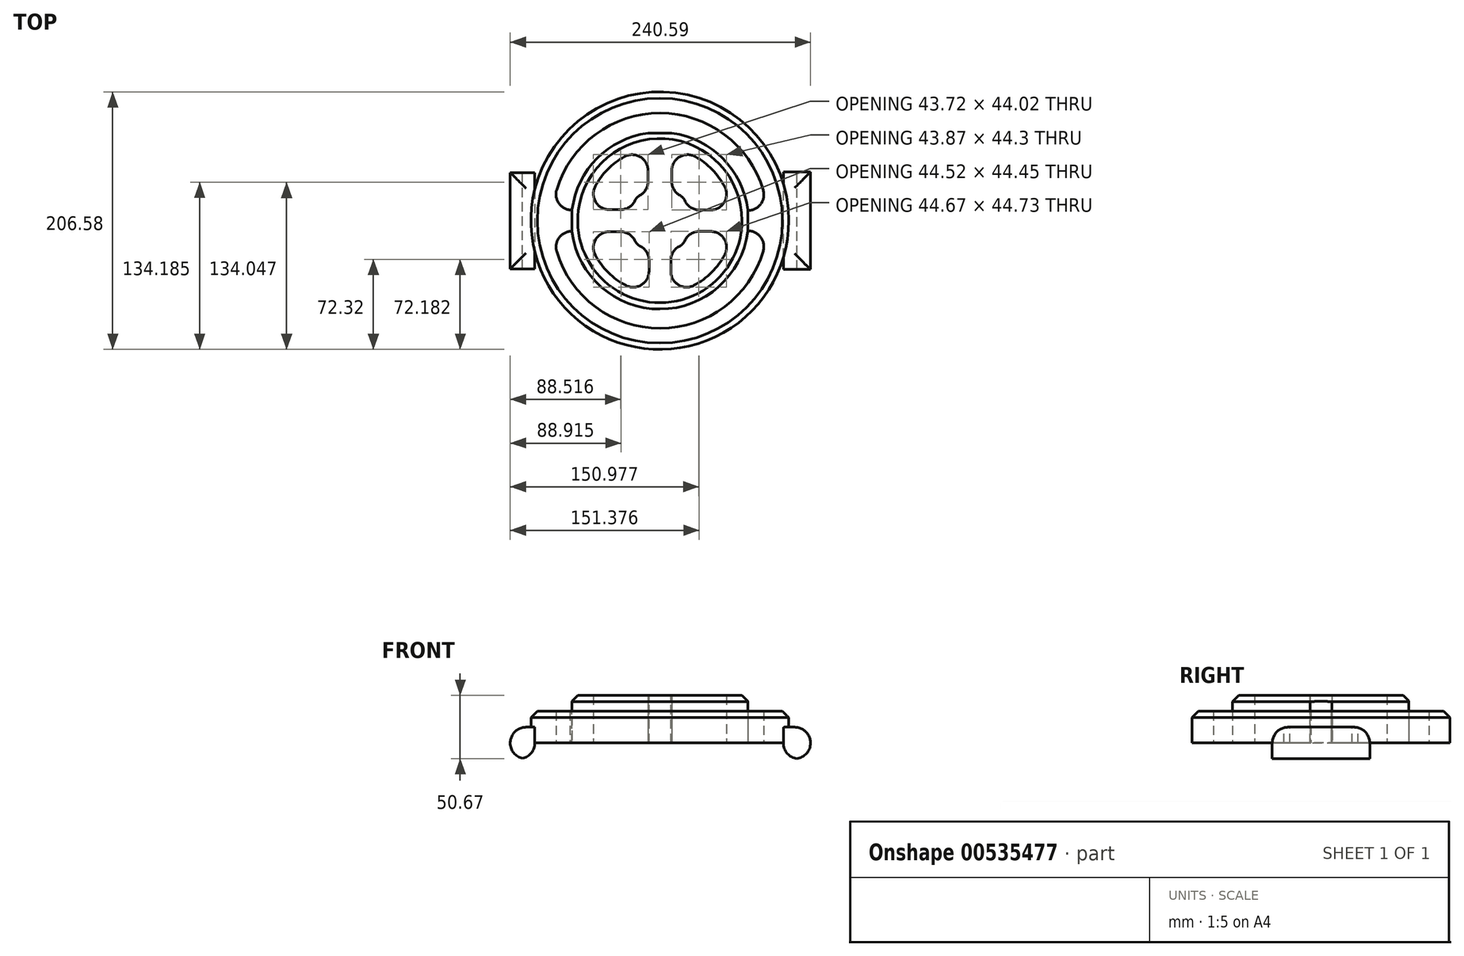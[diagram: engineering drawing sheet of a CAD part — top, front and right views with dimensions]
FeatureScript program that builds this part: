
annotation { "Feature Type Name" : "Feature", "Feature Type Description" : "" }
export const myFeature = defineFeature(function(context is Context, id is Id, definition is map)
    precondition{}
    {
        {
            var Q0;
            Q0=qCreatedBy(makeId("Top.planeOp"),FACE);
            var sketch = newSketch(context, id + "F0", { "sketchPlane" : qUnion([Q0])});
            skCircle(sketch, "E0", {"center": v(0, 0) * mm, "radius": 70.91 * mm});
            skCircle(sketch, "E1", {"center": v(0, 0) * mm, "radius": 58.64 * mm});
            skLineSegment(sketch, "E2.bottom", {"start": v(20.75, 21.47) * mm, "end": v(-20.75, 21.47) * mm});
            skLineSegment(sketch, "E2.top", {"start": v(20.75, -21.47) * mm, "end": v(-20.75, -21.47) * mm});
            skLineSegment(sketch, "E2.left", {"start": v(20.75, 21.47) * mm, "end": v(20.75, -21.47) * mm});
            skLineSegment(sketch, "E2.right", {"start": v(-20.75, 21.47) * mm, "end": v(-20.75, -21.47) * mm});
            skLineSegment(sketch, "E3.bottom", {"start": v(70.4, 8.6) * mm, "end": v(14.78, 8.6) * mm});
            skLineSegment(sketch, "E3.top", {"start": v(70.4, -8.6) * mm, "end": v(14.78, -8.6) * mm});
            skLineSegment(sketch, "E3.left", {"start": v(70.4, 8.6) * mm, "end": v(70.4, -8.6) * mm});
            skLineSegment(sketch, "E3.right", {"start": v(14.78, 8.6) * mm, "end": v(14.78, -8.6) * mm});
            skPoint(sketch, "E3.middle", {"position": v(42.58, 0) * mm});
            skLineSegment(sketch, "E4.bottom", {"start": v(9.53, 70.27) * mm, "end": v(-9.53, 70.27) * mm});
            skLineSegment(sketch, "E4.top", {"start": v(9.53, 11.29) * mm, "end": v(-9.53, 11.29) * mm});
            skLineSegment(sketch, "E4.left", {"start": v(9.53, 70.27) * mm, "end": v(9.53, 11.29) * mm});
            skLineSegment(sketch, "E4.right", {"start": v(-9.53, 70.27) * mm, "end": v(-9.53, 11.29) * mm});
            skPoint(sketch, "E4.middle", {"position": v(0, 40.78) * mm});
            skLineSegment(sketch, "E5.bottom", {"start": v(-70.36, -8.88) * mm, "end": v(-4.76, -8.88) * mm});
            skLineSegment(sketch, "E5.top", {"start": v(-70.36, 8.88) * mm, "end": v(-4.76, 8.88) * mm});
            skLineSegment(sketch, "E5.left", {"start": v(-70.36, -8.88) * mm, "end": v(-70.36, 8.88) * mm});
            skLineSegment(sketch, "E5.right", {"start": v(-4.76, -8.88) * mm, "end": v(-4.76, 8.88) * mm});
            skPoint(sketch, "E5.middle", {"position": v(-37.56, 0) * mm});
            skLineSegment(sketch, "E6.bottom", {"start": v(8.73, -9.64) * mm, "end": v(-8.73, -9.64) * mm});
            skLineSegment(sketch, "E6.top", {"start": v(8.73, -62.55) * mm, "end": v(-8.73, -62.55) * mm});
            skLineSegment(sketch, "E6.left", {"start": v(8.73, -9.64) * mm, "end": v(8.73, -62.55) * mm});
            skLineSegment(sketch, "E6.right", {"start": v(-8.73, -9.64) * mm, "end": v(-8.73, -62.55) * mm});
            skPoint(sketch, "E6.middle", {"position": v(0, -36.1) * mm});
            skPoint(sketch, "E6.middle.positionSnap0", {"position": v(0, -21.47) * mm});
            skPoint(sketch, "E6.centerSnap0", {"position": v(0, -21.47) * mm});
            skSolve(sketch);
        }
        {
            var Q0;
            {var subQ0=sQuery(id+"F0.wireOp",EDGE,"E4.left");var subQ1=sQuery(id+"F0.wireOp",EDGE,"E1");var subQ2=makeQuery(id+"F0.imprint","INTERSECT",VERTEX,{"derivedFrom":[subQ1,subQ0]});Q0=makeQuery(id+"F0.imprint","IMPRINT",FACE,{"disambiguationData":[TD([[makeQuery(id+"F0.imprint","IMPRINT",EDGE,{"disambiguationData":[TD([[subQ2,-1.0]])],"derivedFrom":subQ1}),1.0]])]});}
            var Q1;
            {var subQ5=sQuery(id+"F0.wireOp",EDGE,"E4.bottom");Q1=makeQuery(id+"F0.imprint","IMPRINT",FACE,{"disambiguationData":[TD([[makeQuery(id+"F0.imprint","IMPRINT",EDGE,{"derivedFrom":subQ5}),1.0]])]});}
            var Q2;
            {var subQ3=sQuery(id+"F0.wireOp",EDGE,"E4.left");var subQ5=sQuery(id+"F0.wireOp",EDGE,"E1");var subQ6=makeQuery(id+"F0.imprint","INTERSECT",VERTEX,{"derivedFrom":[subQ5,subQ3]});Q2=makeQuery(id+"F0.imprint","IMPRINT",FACE,{"disambiguationData":[TD([[makeQuery(id+"F0.imprint","IMPRINT",EDGE,{"disambiguationData":[TD([[subQ6,1.0]])],"derivedFrom":subQ5}),-1.0]])]});}
            var Q3;
            {var subQ0=sQuery(id+"F0.wireOp",EDGE,"E4.right");var subQ5=sQuery(id+"F0.wireOp",EDGE,"E1");var subQ6=makeQuery(id+"F0.imprint","INTERSECT",VERTEX,{"derivedFrom":[subQ5,subQ0]});Q3=makeQuery(id+"F0.imprint","IMPRINT",FACE,{"disambiguationData":[TD([[makeQuery(id+"F0.imprint","IMPRINT",EDGE,{"disambiguationData":[TD([[subQ6,-1.0]])],"derivedFrom":subQ5}),-1.0]])]});}
            var Q4;
            {var subQ9=sQuery(id+"F0.wireOp",EDGE,"E6.top");Q4=makeQuery(id+"F0.imprint","IMPRINT",FACE,{"disambiguationData":[TD([[makeQuery(id+"F0.imprint","IMPRINT",EDGE,{"derivedFrom":subQ9}),1.0]])]});}
            var Q5;
            {var subQ0=sQuery(id+"F0.wireOp",EDGE,"E6.right");var subQ1=sQuery(id+"F0.wireOp",EDGE,"E1");var subQ2=makeQuery(id+"F0.imprint","INTERSECT",VERTEX,{"derivedFrom":[subQ1,subQ0]});Q5=makeQuery(id+"F0.imprint","IMPRINT",FACE,{"disambiguationData":[TD([[makeQuery(id+"F0.imprint","IMPRINT",EDGE,{"disambiguationData":[TD([[subQ2,-1.0]])],"derivedFrom":subQ1}),1.0]])]});}
            var Q6;
            {var subQ5=sQuery(id+"F0.wireOp",EDGE,"E6.top");Q6=makeQuery(id+"F0.imprint","IMPRINT",FACE,{"disambiguationData":[TD([[makeQuery(id+"F0.imprint","IMPRINT",EDGE,{"derivedFrom":subQ5}),-1.0]])]});}
            var Q7;
            {var subQ5=sQuery(id+"F0.wireOp",EDGE,"E6.bottom");Q7=makeQuery(id+"F0.imprint","IMPRINT",FACE,{"disambiguationData":[TD([[makeQuery(id+"F0.imprint","IMPRINT",EDGE,{"derivedFrom":subQ5}),1.0]])]});}
            var Q8;
            {var subQ10=sQuery(id+"F0.wireOp",EDGE,"E3.right");Q8=makeQuery(id+"F0.imprint","IMPRINT",FACE,{"disambiguationData":[TD([[makeQuery(id+"F0.imprint","IMPRINT",EDGE,{"derivedFrom":subQ10}),-1.0]])]});}
            var Q9;
            {var subQ5=sQuery(id+"F0.wireOp",EDGE,"E5.right");Q9=makeQuery(id+"F0.imprint","IMPRINT",FACE,{"disambiguationData":[TD([[makeQuery(id+"F0.imprint","IMPRINT",EDGE,{"derivedFrom":subQ5}),1.0]])]});}
            var Q10;
            {var subQ5=sQuery(id+"F0.wireOp",EDGE,"E4.top");Q10=makeQuery(id+"F0.imprint","IMPRINT",FACE,{"disambiguationData":[TD([[makeQuery(id+"F0.imprint","IMPRINT",EDGE,{"derivedFrom":subQ5}),-1.0]])]});}
            var Q11;
            {var subQ0=sQuery(id+"F0.wireOp",EDGE,"E3.bottom");var subQ1=sQuery(id+"F0.wireOp",EDGE,"E1");var subQ2=makeQuery(id+"F0.imprint","INTERSECT",VERTEX,{"derivedFrom":[subQ1,subQ0]});Q11=makeQuery(id+"F0.imprint","IMPRINT",FACE,{"disambiguationData":[TD([[makeQuery(id+"F0.imprint","IMPRINT",EDGE,{"disambiguationData":[TD([[subQ2,1.0]])],"derivedFrom":subQ1}),1.0]])]});}
            var Q12;
            {var subQ5=sQuery(id+"F0.wireOp",EDGE,"E3.right");Q12=makeQuery(id+"F0.imprint","IMPRINT",FACE,{"disambiguationData":[TD([[makeQuery(id+"F0.imprint","IMPRINT",EDGE,{"derivedFrom":subQ5}),1.0]])]});}
            var Q13;
            {var subQ5=sQuery(id+"F0.wireOp",EDGE,"E3.left");Q13=makeQuery(id+"F0.imprint","IMPRINT",FACE,{"disambiguationData":[TD([[makeQuery(id+"F0.imprint","IMPRINT",EDGE,{"derivedFrom":subQ5}),-1.0]])]});}
            var Q14;
            {var subQ5=sQuery(id+"F0.wireOp",EDGE,"E5.left");Q14=makeQuery(id+"F0.imprint","IMPRINT",FACE,{"disambiguationData":[TD([[makeQuery(id+"F0.imprint","IMPRINT",EDGE,{"derivedFrom":subQ5}),-1.0]])]});}
            var Q15;
            {var subQ0=sQuery(id+"F0.wireOp",EDGE,"E5.top");var subQ1=sQuery(id+"F0.wireOp",EDGE,"E1");var subQ2=makeQuery(id+"F0.imprint","INTERSECT",VERTEX,{"derivedFrom":[subQ1,subQ0]});Q15=makeQuery(id+"F0.imprint","IMPRINT",FACE,{"disambiguationData":[TD([[makeQuery(id+"F0.imprint","IMPRINT",EDGE,{"disambiguationData":[TD([[subQ2,-1.0]])],"derivedFrom":subQ1}),1.0]])]});}
            extrude(context, id + "F1", {"entities" : qUnion([Q0, Q1, Q2, Q3, Q4, Q5, Q6, Q7, Q8, Q9, Q10, Q11, Q12, Q13, Q14, Q15]), "depth" : 25.4 * mm, "offsetDistance" : 25.4 * mm});
        }
        {
            var Q0;
            Q0=qCreatedBy(makeId("Top.planeOp"),FACE);
            var sketch = newSketch(context, id + "F2", { "sketchPlane" : qUnion([Q0])});
            skCircle(sketch, "E7", {"center": v(0, 0) * mm, "radius": 86.33 * mm});
            skCircle(sketch, "E8", {"center": v(0, 0) * mm, "radius": 103.3 * mm});
            skLineSegment(sketch, "E9.bottom", {"start": v(94.37, 8.12) * mm, "end": v(61.17, 8.12) * mm});
            skLineSegment(sketch, "E9.top", {"start": v(94.37, -8.12) * mm, "end": v(61.17, -8.12) * mm});
            skLineSegment(sketch, "E9.left", {"start": v(94.37, 8.12) * mm, "end": v(94.37, -8.12) * mm});
            skLineSegment(sketch, "E9.right", {"start": v(61.17, 8.12) * mm, "end": v(61.17, -8.12) * mm});
            skPoint(sketch, "E9.middle", {"position": v(77.77, 0) * mm});
            skLineSegment(sketch, "E10.bottom", {"start": v(-59.19, 8.48) * mm, "end": v(-96, 8.48) * mm});
            skLineSegment(sketch, "E10.top", {"start": v(-59.19, -8.48) * mm, "end": v(-96, -8.48) * mm});
            skLineSegment(sketch, "E10.left", {"start": v(-59.19, 8.48) * mm, "end": v(-59.19, -8.48) * mm});
            skLineSegment(sketch, "E10.right", {"start": v(-96, 8.48) * mm, "end": v(-96, -8.48) * mm});
            skPoint(sketch, "E10.middle", {"position": v(-77.6, 0) * mm});
            skSolve(sketch);
        }
        {
            var Q0;
            Q0=makeQuery(id+"F2.imprint","IMPRINT",FACE,{"disambiguationData":[TD([[makeQuery(id+"F2.imprint","IMPRINT",EDGE,{"derivedFrom":sQuery(id+"F2.wireOp",EDGE,"E8")}),1.0]])]});
            var Q1;
            {var subQ5=sQuery(id+"F2.wireOp",EDGE,"E9.left");Q1=makeQuery(id+"F2.imprint","IMPRINT",FACE,{"disambiguationData":[TD([[makeQuery(id+"F2.imprint","IMPRINT",EDGE,{"derivedFrom":subQ5}),-1.0]])]});}
            var Q2;
            {var subQ5=sQuery(id+"F2.wireOp",EDGE,"E9.right");Q2=makeQuery(id+"F2.imprint","IMPRINT",FACE,{"disambiguationData":[TD([[makeQuery(id+"F2.imprint","IMPRINT",EDGE,{"derivedFrom":subQ5}),1.0]])]});}
            var Q3;
            {var subQ5=sQuery(id+"F2.wireOp",EDGE,"E10.left");Q3=makeQuery(id+"F2.imprint","IMPRINT",FACE,{"disambiguationData":[TD([[makeQuery(id+"F2.imprint","IMPRINT",EDGE,{"derivedFrom":subQ5}),-1.0]])]});}
            var Q4;
            {var subQ5=sQuery(id+"F2.wireOp",EDGE,"E10.right");Q4=makeQuery(id+"F2.imprint","IMPRINT",FACE,{"disambiguationData":[TD([[makeQuery(id+"F2.imprint","IMPRINT",EDGE,{"derivedFrom":subQ5}),1.0]])]});}
            extrude(context, id + "F3", {"entities" : qUnion([Q0, Q1, Q2, Q3, Q4]), "operationType" : NewBodyOperationType.ADD, "depth" : 12.7 * mm, "offsetDistance" : 25.4 * mm});
        }
        {
            var Q0;
            Q0=makeQuery(id+"F1.opExtrude","SWEPT_EDGE",EDGE,{"disambiguationData":[OSD([sQuery(id+"F0.wireOp",EDGE,"E2.top"),sQuery(id+"F0.wireOp",EDGE,"E2.right")])]});
            var Q1;
            Q1=makeQuery(id+"F1.opExtrude","SWEPT_EDGE",EDGE,{"disambiguationData":[OSD([sQuery(id+"F0.wireOp",EDGE,"E2.top"),sQuery(id+"F0.wireOp",EDGE,"E2.left")])]});
            var Q2;
            Q2=makeQuery(id+"F1.opExtrude","SWEPT_EDGE",EDGE,{"disambiguationData":[OSD([sQuery(id+"F0.wireOp",EDGE,"E2.bottom"),sQuery(id+"F0.wireOp",EDGE,"E2.left")])]});
            var Q3;
            Q3=makeQuery(id+"F1.opExtrude","SWEPT_EDGE",EDGE,{"disambiguationData":[OSD([sQuery(id+"F0.wireOp",EDGE,"E2.bottom"),sQuery(id+"F0.wireOp",EDGE,"E2.right")])]});
            fillet(context, id + "F4", {"entities" : qUnion([Q0, Q1, Q2, Q3]), "radius" : 9.16 * mm, "tangentPropagation" : true, "allowEdgeOverflow" : false});
        }
        {
            var Q0;
            Q0=makeQuery(id+"F1.opExtrude","SWEPT_EDGE",EDGE,{"disambiguationData":[OSD([sQuery(id+"F0.wireOp",EDGE,"E1"),sQuery(id+"F0.wireOp",EDGE,"E4.left")])]});
            var Q1;
            Q1=makeQuery(id+"F1.opExtrude","SWEPT_EDGE",EDGE,{"disambiguationData":[OSD([sQuery(id+"F0.wireOp",EDGE,"E1"),sQuery(id+"F0.wireOp",EDGE,"E3.bottom")])]});
            var Q2;
            Q2=makeQuery(id+"F1.opExtrude","SWEPT_EDGE",EDGE,{"disambiguationData":[OSD([sQuery(id+"F0.wireOp",EDGE,"E1"),sQuery(id+"F0.wireOp",EDGE,"E4.right")])]});
            var Q3;
            Q3=makeQuery(id+"F1.opExtrude","SWEPT_EDGE",EDGE,{"disambiguationData":[OSD([sQuery(id+"F0.wireOp",EDGE,"E1"),sQuery(id+"F0.wireOp",EDGE,"E5.top")])]});
            var Q4;
            Q4=makeQuery(id+"F1.opExtrude","SWEPT_EDGE",EDGE,{"disambiguationData":[OSD([sQuery(id+"F0.wireOp",EDGE,"E1"),sQuery(id+"F0.wireOp",EDGE,"E3.top")])]});
            var Q5;
            Q5=makeQuery(id+"F1.opExtrude","SWEPT_EDGE",EDGE,{"disambiguationData":[OSD([sQuery(id+"F0.wireOp",EDGE,"E1"),sQuery(id+"F0.wireOp",EDGE,"E6.left")])]});
            var Q6;
            Q6=makeQuery(id+"F1.opExtrude","SWEPT_EDGE",EDGE,{"disambiguationData":[OSD([sQuery(id+"F0.wireOp",EDGE,"E1"),sQuery(id+"F0.wireOp",EDGE,"E5.bottom")])]});
            var Q7;
            Q7=makeQuery(id+"F1.opExtrude","SWEPT_EDGE",EDGE,{"disambiguationData":[OSD([sQuery(id+"F0.wireOp",EDGE,"E1"),sQuery(id+"F0.wireOp",EDGE,"E6.right")])]});
            var Q8;
            Q8=makeQuery(id+"F1.opExtrude","SWEPT_EDGE",EDGE,{"disambiguationData":[OSD([sQuery(id+"F0.wireOp",EDGE,"E2.right"),sQuery(id+"F0.wireOp",EDGE,"E5.bottom")])]});
            var Q9;
            Q9=makeQuery(id+"F1.opExtrude","SWEPT_EDGE",EDGE,{"disambiguationData":[OSD([sQuery(id+"F0.wireOp",EDGE,"E2.top"),sQuery(id+"F0.wireOp",EDGE,"E6.right")])]});
            var Q10;
            Q10=makeQuery(id+"F1.opExtrude","SWEPT_EDGE",EDGE,{"disambiguationData":[OSD([sQuery(id+"F0.wireOp",EDGE,"E2.left"),sQuery(id+"F0.wireOp",EDGE,"E3.top")])]});
            var Q11;
            Q11=makeQuery(id+"F1.opExtrude","SWEPT_EDGE",EDGE,{"disambiguationData":[OSD([sQuery(id+"F0.wireOp",EDGE,"E2.top"),sQuery(id+"F0.wireOp",EDGE,"E6.left")])]});
            var Q12;
            Q12=makeQuery(id+"F1.opExtrude","SWEPT_EDGE",EDGE,{"disambiguationData":[OSD([sQuery(id+"F0.wireOp",EDGE,"E2.bottom"),sQuery(id+"F0.wireOp",EDGE,"E4.left")])]});
            var Q13;
            Q13=makeQuery(id+"F1.opExtrude","SWEPT_EDGE",EDGE,{"disambiguationData":[OSD([sQuery(id+"F0.wireOp",EDGE,"E2.left"),sQuery(id+"F0.wireOp",EDGE,"E3.bottom")])]});
            var Q14;
            Q14=makeQuery(id+"F1.opExtrude","SWEPT_EDGE",EDGE,{"disambiguationData":[OSD([sQuery(id+"F0.wireOp",EDGE,"E2.right"),sQuery(id+"F0.wireOp",EDGE,"E5.top")])]});
            var Q15;
            Q15=makeQuery(id+"F1.opExtrude","SWEPT_EDGE",EDGE,{"disambiguationData":[OSD([sQuery(id+"F0.wireOp",EDGE,"E2.bottom"),sQuery(id+"F0.wireOp",EDGE,"E4.right")])]});
            var Q16;
            Q16=makeQuery(id+"F3.opExtrude","SWEPT_EDGE",EDGE,{"disambiguationData":[OSD([sQuery(id+"F2.wireOp",EDGE,"E7"),sQuery(id+"F2.wireOp",EDGE,"E9.top")])]});
            var Q17;
            Q17=makeQuery(id+"F3.opExtrude","SWEPT_EDGE",EDGE,{"disambiguationData":[OSD([sQuery(id+"F2.wireOp",EDGE,"E7"),sQuery(id+"F2.wireOp",EDGE,"E10.top")])]});
            var Q18;
            Q18=makeQuery(id+"F3.boolean.opBoolean","INTERSECT",EDGE,{"derivedFrom":[makeQuery(id+"F1.opExtrude","SWEPT_FACE",FACE,{"disambiguationData":[OSD([sQuery(id+"F0.wireOp",EDGE,"E5.left")])]}),makeQuery(id+"F3.opExtrude","SWEPT_FACE",FACE,{"disambiguationData":[OSD([sQuery(id+"F2.wireOp",EDGE,"E10.top")])]})]});
            var Q19;
            Q19=makeQuery(id+"F3.opExtrude","SWEPT_EDGE",EDGE,{"disambiguationData":[OSD([sQuery(id+"F2.wireOp",EDGE,"E7"),sQuery(id+"F2.wireOp",EDGE,"E10.bottom")])]});
            var Q20;
            Q20=makeQuery(id+"F3.opExtrude","SWEPT_EDGE",EDGE,{"disambiguationData":[OSD([sQuery(id+"F2.wireOp",EDGE,"E7"),sQuery(id+"F2.wireOp",EDGE,"E9.bottom")])]});
            fillet(context, id + "F5", {"entities" : qUnion([Q0, Q1, Q2, Q3, Q4, Q5, Q6, Q7, Q8, Q9, Q10, Q11, Q12, Q13, Q14, Q15, Q16, Q17, Q18, Q19, Q20]), "radius" : 12.7 * mm, "tangentPropagation" : true, "allowEdgeOverflow" : false});
        }
        {
            var Q0;
            Q0=qCreatedBy(makeId("Top.planeOp"),FACE);
            var sketch = newSketch(context, id + "F6", { "sketchPlane" : qUnion([Q0])});
            skLineSegment(sketch, "E11.bottom", {"start": v(120.68, -39.1) * mm, "end": v(98.93, -39.1) * mm});
            skLineSegment(sketch, "E11.top", {"start": v(120.68, 39.1) * mm, "end": v(98.93, 39.1) * mm});
            skLineSegment(sketch, "E11.left", {"start": v(120.68, -39.1) * mm, "end": v(120.68, 39.1) * mm});
            skLineSegment(sketch, "E11.right", {"start": v(98.93, -39.1) * mm, "end": v(98.93, 39.1) * mm});
            skPoint(sketch, "E11.middle", {"position": v(109.8, 0) * mm});
            skLineSegment(sketch, "E12.bottom", {"start": v(-119.9, 38.59) * mm, "end": v(-100.22, 38.59) * mm});
            skLineSegment(sketch, "E12.top", {"start": v(-119.9, -38.59) * mm, "end": v(-100.22, -38.59) * mm});
            skLineSegment(sketch, "E12.left", {"start": v(-119.9, 38.59) * mm, "end": v(-119.9, -38.59) * mm});
            skLineSegment(sketch, "E12.right", {"start": v(-100.22, 38.59) * mm, "end": v(-100.22, -38.59) * mm});
            skPoint(sketch, "E12.middle", {"position": v(-110.07, 0) * mm});
            skSolve(sketch);
        }
        {
            var Q0;
            Q0=makeQuery(id+"F6.imprint","IMPRINT",FACE,{"disambiguationData":[TD([[makeQuery(id+"F6.imprint","IMPRINT",EDGE,{"derivedFrom":sQuery(id+"F6.wireOp",EDGE,"E11.bottom")}),-1.0]])]});
            var Q1;
            Q1=makeQuery(id+"F6.imprint","IMPRINT",FACE,{"disambiguationData":[TD([[makeQuery(id+"F6.imprint","IMPRINT",EDGE,{"derivedFrom":sQuery(id+"F6.wireOp",EDGE,"E12.bottom")}),-1.0]])]});
            extrude(context, id + "F7", {"entities" : qUnion([Q0, Q1]), "operationType" : NewBodyOperationType.ADD, "oppositeDirection" : true, "depth" : 25.4 * mm, "offsetDistance" : 25.4 * mm});
        }
        {
            var Q0;
            Q0=makeQuery(id+"F7.opExtrude","CAP_EDGE",EDGE,{"disambiguationData":[OSD([sQuery(id+"F6.wireOp",EDGE,"E12.left")])],"isStart":false});
            var Q1;
            Q1=makeQuery(id+"F7.opExtrude","CAP_EDGE",EDGE,{"disambiguationData":[OSD([sQuery(id+"F6.wireOp",EDGE,"E12.right")])],"isStart":false});
            var Q2;
            Q2=makeQuery(id+"F7.opExtrude","CAP_EDGE",EDGE,{"disambiguationData":[OSD([sQuery(id+"F6.wireOp",EDGE,"E12.bottom")])],"isStart":true});
            var Q3;
            Q3=makeQuery(id+"F7.opExtrude","CAP_EDGE",EDGE,{"disambiguationData":[OSD([sQuery(id+"F6.wireOp",EDGE,"E12.top")])],"isStart":true});
            var Q4;
            Q4=makeQuery(id+"F7.opExtrude","CAP_EDGE",EDGE,{"disambiguationData":[OSD([sQuery(id+"F6.wireOp",EDGE,"E12.left")])],"isStart":true});
            var Q5;
            Q5=makeQuery(id+"F7.opExtrude","CAP_EDGE",EDGE,{"disambiguationData":[OSD([sQuery(id+"F6.wireOp",EDGE,"E11.right")])],"isStart":false});
            var Q6;
            Q6=makeQuery(id+"F7.opExtrude","CAP_EDGE",EDGE,{"disambiguationData":[OSD([sQuery(id+"F6.wireOp",EDGE,"E11.left")])],"isStart":false});
            var Q7;
            Q7=makeQuery(id+"F7.opExtrude","CAP_EDGE",EDGE,{"disambiguationData":[OSD([sQuery(id+"F6.wireOp",EDGE,"E11.bottom")])],"isStart":true});
            var Q8;
            Q8=makeQuery(id+"F7.opExtrude","CAP_EDGE",EDGE,{"disambiguationData":[OSD([sQuery(id+"F6.wireOp",EDGE,"E11.left")])],"isStart":true});
            var Q9;
            Q9=makeQuery(id+"F7.opExtrude","CAP_EDGE",EDGE,{"disambiguationData":[OSD([sQuery(id+"F6.wireOp",EDGE,"E11.top")])],"isStart":true});
            fillet(context, id + "F8", {"entities" : qUnion([Q0, Q1, Q2, Q3, Q4, Q5, Q6, Q7, Q8, Q9]), "radius" : 12.7 * mm, "tangentPropagation" : true, "allowEdgeOverflow" : false});
        }
        {
            var Q0;
            Q0=makeQuery(id+"F3.opExtrude","CAP_EDGE",EDGE,{"disambiguationData":[OSD([sQuery(id+"F2.wireOp",EDGE,"E8")])],"isStart":false});
            var Q1;
            {var subQ0=sQuery(id+"F0.wireOp",EDGE,"E0");Q1=makeQuery(id+"F1.opExtrude","CAP_EDGE",EDGE,{"disambiguationData":[OSD([subQ0]),TDD([makeQuery(id+"F0.imprint","IMPRINT",EDGE,{"disambiguationData":[TD([[makeQuery(id+"F0.imprint","INTERSECT",VERTEX,{"derivedFrom":[subQ0,sQuery(id+"F0.wireOp",EDGE,"E3.bottom"),sQuery(id+"F0.wireOp",EDGE,"E3.left")]}),-1.0]])],"derivedFrom":subQ0})])],"isStart":false});}
            chamfer(context, id + "F9", {"entities" : qUnion([Q0, Q1]), "width" : 5.08 * mm, "tangentPropagation" : true});
        }
        {
            var Q0;
            Q0=makeQuery(id+"F3.boolean.opBoolean","MERGE",FACE,{"derivedFrom":[makeQuery(id+"F1.opExtrude","CAP_FACE",FACE,{"disambiguationData":[OSD([sQuery(id+"F0.wireOp",EDGE,"E0"),sQuery(id+"F0.wireOp",EDGE,"E1"),sQuery(id+"F0.wireOp",EDGE,"E2.bottom"),sQuery(id+"F0.wireOp",EDGE,"E2.top"),sQuery(id+"F0.wireOp",EDGE,"E2.left"),sQuery(id+"F0.wireOp",EDGE,"E2.right"),sQuery(id+"F0.wireOp",EDGE,"E3.bottom"),sQuery(id+"F0.wireOp",EDGE,"E3.top"),sQuery(id+"F0.wireOp",EDGE,"E3.left"),sQuery(id+"F0.wireOp",EDGE,"E4.bottom"),sQuery(id+"F0.wireOp",EDGE,"E4.left"),sQuery(id+"F0.wireOp",EDGE,"E4.right"),sQuery(id+"F0.wireOp",EDGE,"E5.bottom"),sQuery(id+"F0.wireOp",EDGE,"E5.top"),sQuery(id+"F0.wireOp",EDGE,"E5.left"),sQuery(id+"F0.wireOp",EDGE,"E6.left"),sQuery(id+"F0.wireOp",EDGE,"E6.right")])],"isStart":true}),makeQuery(id+"F3.opExtrude","CAP_FACE",FACE,{"disambiguationData":[OSD([sQuery(id+"F2.wireOp",EDGE,"E7"),sQuery(id+"F2.wireOp",EDGE,"E8"),sQuery(id+"F2.wireOp",EDGE,"E9.bottom"),sQuery(id+"F2.wireOp",EDGE,"E9.top"),sQuery(id+"F2.wireOp",EDGE,"E9.right"),sQuery(id+"F2.wireOp",EDGE,"E10.bottom"),sQuery(id+"F2.wireOp",EDGE,"E10.top"),sQuery(id+"F2.wireOp",EDGE,"E10.left")])],"isStart":true})]});
            extrude(context, id + "F10", {"entities" : qUnion([Q0]), "operationType" : NewBodyOperationType.ADD, "depth" : 12.7 * mm, "offsetDistance" : 25.4 * mm});
        }
    });
